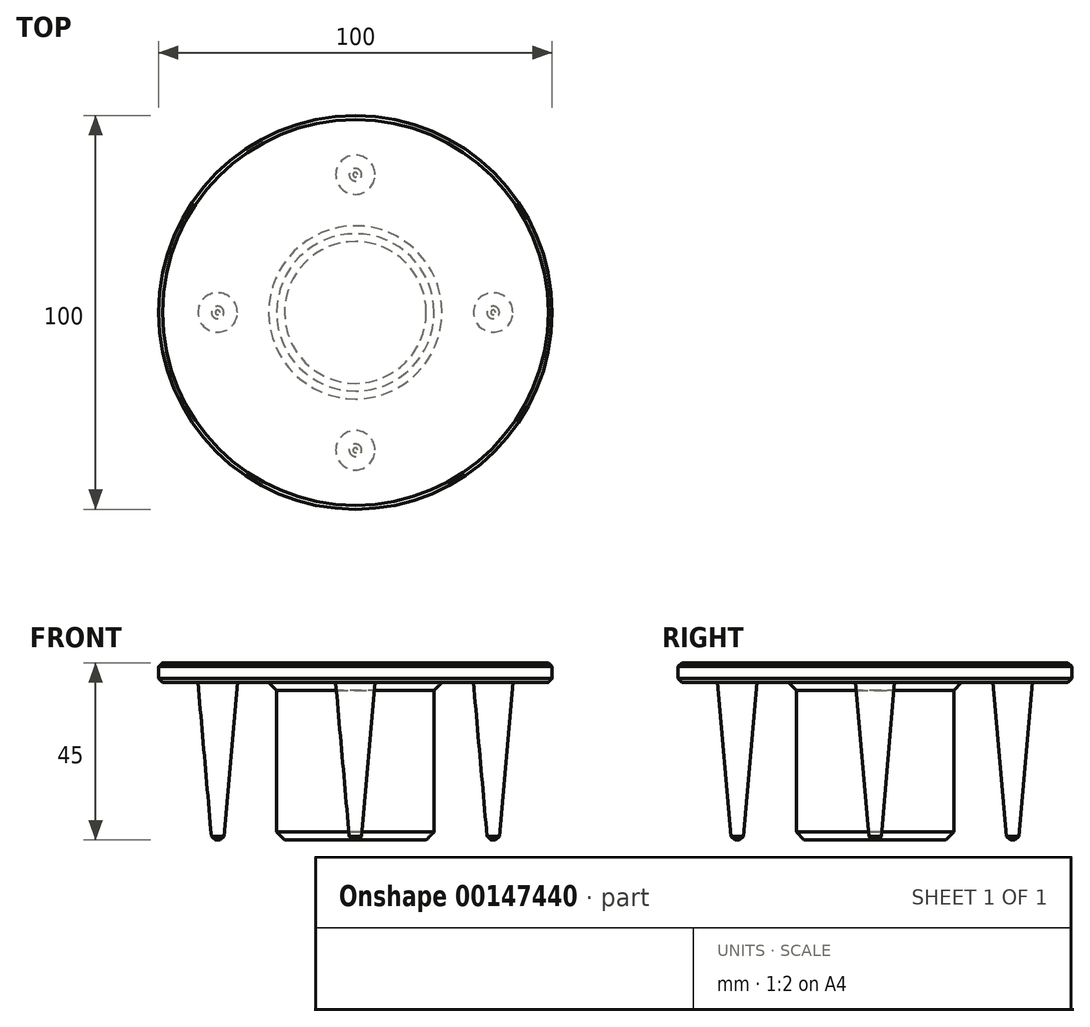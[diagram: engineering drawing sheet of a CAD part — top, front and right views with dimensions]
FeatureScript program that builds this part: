
annotation { "Feature Type Name" : "Feature", "Feature Type Description" : "" }
export const myFeature = defineFeature(function(context is Context, id is Id, definition is map)
    precondition{}
    {
        {
            var Q0;
            Q0=qCreatedBy(makeId("Front.planeOp"),FACE);
            var sketch = newSketch(context, id + "F0", { "sketchPlane" : qUnion([Q0])});
            skLineSegment(sketch, "E0", {"start": v(0, 0) * mm, "end": v(-50, 0) * mm});
            skLineSegment(sketch, "E1", {"start": v(-50, 0) * mm, "end": v(-50, -5) * mm});
            skLineSegment(sketch, "E2", {"start": v(-50, -5) * mm, "end": v(-20, -5) * mm});
            skLineSegment(sketch, "E3", {"start": v(-20, -5) * mm, "end": v(-20, -45) * mm});
            skLineSegment(sketch, "E4", {"start": v(-20, -45) * mm, "end": v(0, -45) * mm});
            skLineSegment(sketch, "E5", {"start": v(0, -45) * mm, "end": v(0, 0) * mm});
            skSolve(sketch);
        }
        {
            var Q0;
            Q0=makeQuery(id+"F0.imprint","IMPRINT",FACE,{"disambiguationData":[TD([[makeQuery(id+"F0.imprint","IMPRINT",EDGE,{"derivedFrom":sQuery(id+"F0.wireOp",EDGE,"E0")}),1.0]])]});
            var Q1;
            Q1=sQuery(id+"F0.wireOp",EDGE,"E5");
            revolve(context, id + "F1", {"entities" : qUnion([Q0]), "axis" : qUnion([Q1]), "revolveType" : RevolveType.FULL});
        }
        {
            var Q0;
            Q0=makeQuery(id+"F1.opRevolve","SWEPT_FACE",FACE,{"disambiguationData":[OSD([sQuery(id+"F0.wireOp",EDGE,"E2")])]});
            var sketch = newSketch(context, id + "F2", { "sketchPlane" : qUnion([Q0])});
            skCircle(sketch, "E6", {"center": v(0, 35) * mm, "radius": 5 * mm});
            skCircle(sketch, "E7", {"center": v(-35, 0) * mm, "radius": 5 * mm});
            skCircle(sketch, "E8", {"center": v(35, 0) * mm, "radius": 5 * mm});
            skCircle(sketch, "E9", {"center": v(0, -35) * mm, "radius": 5 * mm});
            skSolve(sketch);
        }
        {
            var Q0;
            Q0=makeQuery(id+"F1.opRevolve","SWEPT_FACE",FACE,{"disambiguationData":[OSD([sQuery(id+"F0.wireOp",EDGE,"E4")])]});
            var sketch = newSketch(context, id + "F3", { "sketchPlane" : qUnion([Q0])});
            skCircle(sketch, "E10", {"center": v(-35, 0) * mm, "radius": 1.5 * mm});
            skCircle(sketch, "E11", {"center": v(0, 35) * mm, "radius": 1.5 * mm});
            skCircle(sketch, "E12", {"center": v(35, 0) * mm, "radius": 1.5 * mm});
            skCircle(sketch, "E13", {"center": v(0, -35) * mm, "radius": 1.5 * mm});
            skSolve(sketch);
        }
        {
            var Q1;
            Q1=makeQuery(id+"F3.imprint","IMPRINT",FACE,{"disambiguationData":[TD([[makeQuery(id+"F3.imprint","IMPRINT",EDGE,{"derivedFrom":sQuery(id+"F3.wireOp",EDGE,"E10")}),1.0]])]});
            var Q2;
            Q2=makeQuery(id+"F2.imprint","IMPRINT",FACE,{"disambiguationData":[TD([[makeQuery(id+"F2.imprint","IMPRINT",EDGE,{"derivedFrom":sQuery(id+"F2.wireOp",EDGE,"E7")}),1.0]])]});
            loft(context, id + "F4", {"operationType" : NewBodyOperationType.ADD, "sheetProfilesArray" : [{ "sheetProfileEntities" : qUnion([Q1]) }, { "sheetProfileEntities" : qUnion([Q2]) }]});
        }
        {
            var Q1;
            Q1=makeQuery(id+"F2.imprint","IMPRINT",FACE,{"disambiguationData":[TD([[makeQuery(id+"F2.imprint","IMPRINT",EDGE,{"derivedFrom":sQuery(id+"F2.wireOp",EDGE,"E9")}),1.0]])]});
            var Q2;
            Q2=makeQuery(id+"F3.imprint","IMPRINT",FACE,{"disambiguationData":[TD([[makeQuery(id+"F3.imprint","IMPRINT",EDGE,{"derivedFrom":sQuery(id+"F3.wireOp",EDGE,"E13")}),1.0]])]});
            loft(context, id + "F5", {"operationType" : NewBodyOperationType.ADD, "sheetProfilesArray" : [{ "sheetProfileEntities" : qUnion([Q1]) }, { "sheetProfileEntities" : qUnion([Q2]) }]});
        }
        {
            var Q1;
            Q1=makeQuery(id+"F2.imprint","IMPRINT",FACE,{"disambiguationData":[TD([[makeQuery(id+"F2.imprint","IMPRINT",EDGE,{"derivedFrom":sQuery(id+"F2.wireOp",EDGE,"E8")}),1.0]])]});
            var Q2;
            Q2=makeQuery(id+"F3.imprint","IMPRINT",FACE,{"disambiguationData":[TD([[makeQuery(id+"F3.imprint","IMPRINT",EDGE,{"derivedFrom":sQuery(id+"F3.wireOp",EDGE,"E12")}),1.0]])]});
            loft(context, id + "F6", {"operationType" : NewBodyOperationType.ADD, "sheetProfilesArray" : [{ "sheetProfileEntities" : qUnion([Q1]) }, { "sheetProfileEntities" : qUnion([Q2]) }]});
        }
        {
            var Q1;
            Q1=makeQuery(id+"F3.imprint","IMPRINT",FACE,{"disambiguationData":[TD([[makeQuery(id+"F3.imprint","IMPRINT",EDGE,{"derivedFrom":sQuery(id+"F3.wireOp",EDGE,"E11")}),1.0]])]});
            var Q2;
            Q2=makeQuery(id+"F2.imprint","IMPRINT",FACE,{"disambiguationData":[TD([[makeQuery(id+"F2.imprint","IMPRINT",EDGE,{"derivedFrom":sQuery(id+"F2.wireOp",EDGE,"E6")}),1.0]])]});
            loft(context, id + "F7", {"operationType" : NewBodyOperationType.ADD, "sheetProfilesArray" : [{ "sheetProfileEntities" : qUnion([Q1]) }, { "sheetProfileEntities" : qUnion([Q2]) }]});
        }
        {
            var Q0;
            Q0=makeQuery(id+"F1.opRevolve","SWEPT_EDGE",EDGE,{"disambiguationData":[OSD([sQuery(id+"F0.wireOp",EDGE,"E3"),sQuery(id+"F0.wireOp",EDGE,"E4")])]});
            var Q1;
            Q1=makeQuery(id+"F1.opRevolve","SWEPT_EDGE",EDGE,{"disambiguationData":[OSD([sQuery(id+"F0.wireOp",EDGE,"E2"),sQuery(id+"F0.wireOp",EDGE,"E3")])]});
            var Q2;
            Q2=makeQuery(id+"F6.opLoft","MID_CAP_EDGE",EDGE,{"disambiguationData":[OSD([sQuery(id+"F2.wireOp",EDGE,"E8")])],"capPos":0.0});
            var Q3;
            Q3=makeQuery(id+"F5.opLoft","MID_CAP_EDGE",EDGE,{"disambiguationData":[OSD([sQuery(id+"F2.wireOp",EDGE,"E9")])],"capPos":0.0});
            var Q4;
            Q4=makeQuery(id+"F4.opLoft","MID_CAP_EDGE",EDGE,{"disambiguationData":[OSD([sQuery(id+"F2.wireOp",EDGE,"E7"),sQuery(id+"F3.wireOp",EDGE,"E10")])],"capPos":1.0});
            var Q5;
            Q5=makeQuery(id+"F7.opLoft","MID_CAP_EDGE",EDGE,{"disambiguationData":[OSD([sQuery(id+"F2.wireOp",EDGE,"E6"),sQuery(id+"F3.wireOp",EDGE,"E11")])],"capPos":1.0});
            chamfer(context, id + "F8", {"entities" : qUnion([Q0, Q1, Q2, Q3, Q4, Q5]), "width" : 2 * mm, "tangentPropagation" : true});
        }
        {
            var Q0;
            Q0=makeQuery(id+"F1.opRevolve","SWEPT_EDGE",EDGE,{"disambiguationData":[OSD([sQuery(id+"F0.wireOp",EDGE,"E1"),sQuery(id+"F0.wireOp",EDGE,"E2")])]});
            var Q1;
            Q1=makeQuery(id+"F1.opRevolve","SWEPT_EDGE",EDGE,{"disambiguationData":[OSD([sQuery(id+"F0.wireOp",EDGE,"E0"),sQuery(id+"F0.wireOp",EDGE,"E1")])]});
            var Q2;
            Q2=makeQuery(id+"F7.opLoft","MID_CAP_EDGE",EDGE,{"disambiguationData":[OSD([sQuery(id+"F3.wireOp",EDGE,"E11")])],"capPos":0.0});
            var Q3;
            Q3=makeQuery(id+"F4.opLoft","MID_CAP_EDGE",EDGE,{"disambiguationData":[OSD([sQuery(id+"F3.wireOp",EDGE,"E10")])],"capPos":0.0});
            var Q4;
            Q4=makeQuery(id+"F5.opLoft","MID_CAP_EDGE",EDGE,{"disambiguationData":[OSD([sQuery(id+"F2.wireOp",EDGE,"E9"),sQuery(id+"F3.wireOp",EDGE,"E13")])],"capPos":1.0});
            var Q5;
            Q5=makeQuery(id+"F6.opLoft","MID_CAP_EDGE",EDGE,{"disambiguationData":[OSD([sQuery(id+"F2.wireOp",EDGE,"E8"),sQuery(id+"F3.wireOp",EDGE,"E12")])],"capPos":1.0});
            chamfer(context, id + "F9", {"entities" : qUnion([Q0, Q1, Q2, Q3, Q4, Q5]), "width" : 1 * mm, "tangentPropagation" : true});
        }
    });
